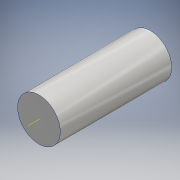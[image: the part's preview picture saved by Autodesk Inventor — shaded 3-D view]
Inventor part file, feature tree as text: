
AUTODESK INVENTOR PART (.ipt)
format: ipt  version: 2016 (Build 200138000, 138)  size: 92,160 bytes
history: native  units: mm
features: extrude x1, other x1, sketch x1
ambient origin geometry x8: Origin, YZ Plane, XZ Plane, XY Plane, X Axis, Y Axis, Z Axis, Center Point
bodies: Solid1 (feature_tree)
feature tree (3):
  extrude  "Extrusion1"  Depth=12.0mm TaperAngle=0.0deg
  other  "Work Axis1"
  sketch  "Sketch1"  dims[d0=4.6mm d1=12.0mm d2=0.0mm]
